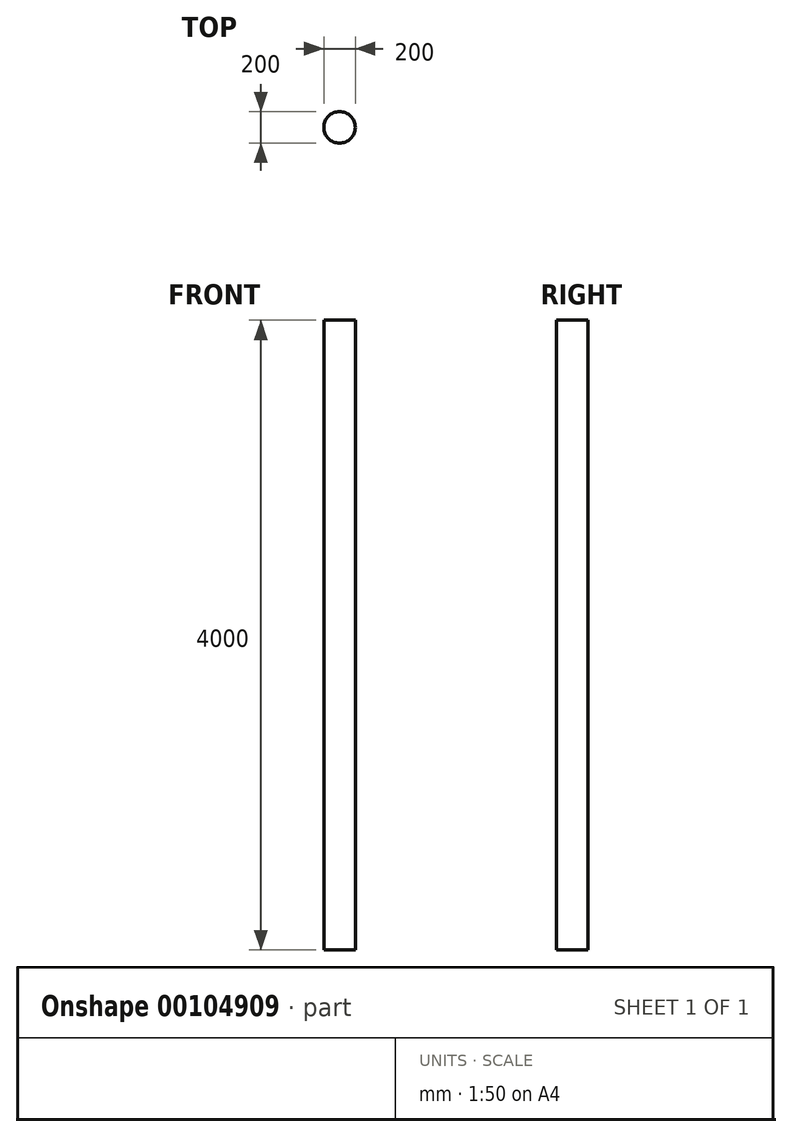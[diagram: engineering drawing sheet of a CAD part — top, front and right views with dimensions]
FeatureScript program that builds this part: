
annotation { "Feature Type Name" : "Feature", "Feature Type Description" : "" }
export const myFeature = defineFeature(function(context is Context, id is Id, definition is map)
    precondition{}
    {
        {
            var Q0;
            Q0=qCreatedBy(makeId("Top.planeOp"),FACE);
            var sketch = newSketch(context, id + "F0", { "sketchPlane" : qUnion([Q0])});
            skCircle(sketch, "E0", {"center": v(0, 0) * mm, "radius": 100 * mm});
            skSolve(sketch);
        }
        {
            var Q0;
            Q0=qSketchRegion(id+"F0",true);
            extrude(context, id + "F1", {"entities" : qUnion([Q0]), "depth" : 4000 * mm});
        }
    });
